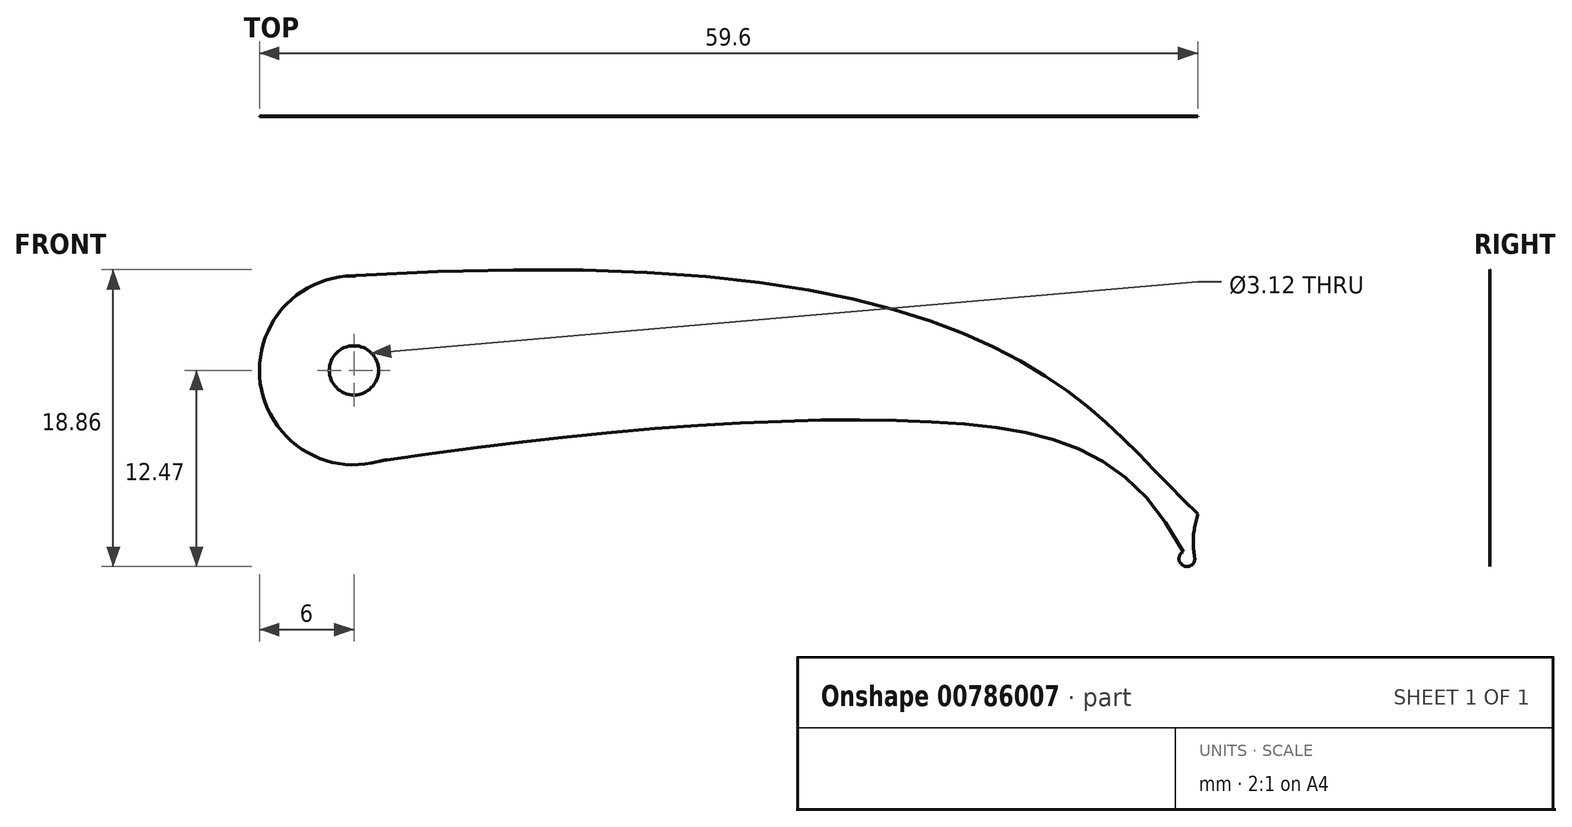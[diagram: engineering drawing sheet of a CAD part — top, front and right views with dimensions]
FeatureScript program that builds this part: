
annotation { "Feature Type Name" : "Feature", "Feature Type Description" : "" }
export const myFeature = defineFeature(function(context is Context, id is Id, definition is map)
    precondition{}
    {
        {
            var Q0;
            Q0=qCreatedBy(makeId("Front.planeOp"),FACE);
            var sketch = newSketch(context, id + "F0", { "sketchPlane" : qUnion([Q0])});
            skCircle(sketch, "E0", {"center": v(0, 0) * mm, "radius": 1.56 * mm});
            skCircle(sketch, "E1", {"center": v(0, 0) * mm, "radius": 6 * mm});
            skFitSpline(sketch, "E2", {"points": [v(0, -6) * mm, v(37.86, -3.33) * mm, v(52.9, -11.97) * mm], "startDerivative": vector(68.13, 10.58) * mm, "endDerivative": vector(25.48, -50.73) * mm});
            skFitSpline(sketch, "E3", {"points": [v(0, 6) * mm, v(53.6, -9.12) * mm], "startDerivative": vector(124.52, 7.86) * mm, "endDerivative": vector(21.52, -20.12) * mm});
            skLineSegment(sketch, "E4", {"start": v(52.9, -11.97) * mm, "end": v(53.6, -9.12) * mm});
            skCircle(sketch, "E5", {"center": v(52.9, -11.97) * mm, "radius": 0.5 * mm});
            skSolve(sketch);
        }
        {
            var Q0;
            Q0=qSketchRegion(id+"F0",true);
            extrude(context, id + "F1", {"entities" : qUnion([Q0]), "depth" : 1 / 203.2 * mm, "offsetDistance" : 25 * mm});
        }
        {
            var Q0;
            Q0=makeQuery(id+"F1.opExtrude","SWEPT_EDGE",EDGE,{"disambiguationData":[OSD([sQuery(id+"F0.wireOp",EDGE,"E1"),sQuery(id+"F0.wireOp",EDGE,"bf37a709-5e8d-4281-9997-04b553430052")])]});
            fillet(context, id + "F2", {"entities" : qUnion([Q0]), "radius" : 5 * mm, "tangentPropagation" : true, "allowEdgeOverflow" : false});
        }
        {
            var Q0;
            Q0=makeQuery(id+"F1.opExtrude","SWEPT_EDGE",EDGE,{"disambiguationData":[OSD([sQuery(id+"F0.wireOp",EDGE,"E4"),sQuery(id+"F0.wireOp",EDGE,"E5")])]});
            fillet(context, id + "F3", {"entities" : qUnion([Q0]), "radius" : 5 * mm, "tangentPropagation" : true, "allowEdgeOverflow" : false});
        }
    });
